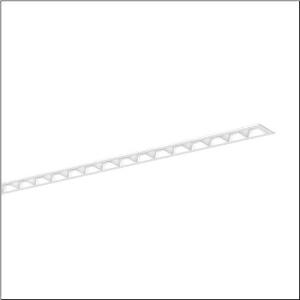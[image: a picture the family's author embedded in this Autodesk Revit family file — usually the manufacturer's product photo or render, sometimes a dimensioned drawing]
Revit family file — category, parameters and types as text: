
# Revit family: silica_r__21_51mx16db45wb_49d2
name_source: partatom
category: Lighting Fixtures
units: mm (PartAtom-declared; Revit-internal decimal feet)

## family parameters
Cut with Voids When Loaded = No
Host = Face
Light Source = No
Part Type = Normal
Room Calculation Point = No
Round Connector Dimension = Use Diameter
Shared = No

## types (1)
- --- (1 x LED, 5400 lm, 29.3 W, 4000K)
    Apparent Load = 29 VA
    CIE Flux Codes = 83 98 100 100 100
    Color Rendering = 80
    Color Temperature = 4000K
    Default Elevation = 1800 mm
    Description = Silica® 21, office luminaire, primary light control with darklight reflector, of PMMA, white, CAT 2 (L<= 3000cd/m²), light emission: direct distribution, primary light characteristic: symmetric, installation type: recessed, LED, rated luminous flux: 5.400lm, luminous efficacy: 184lm/W, light colour: 840, colour temperature: 4000K, with terminal, 3+2-pole, max. 2.5mm², mains connection: 220..240V, AC, 50/60Hz, rated input power: 29.3W, luminaire housing, of aluminium, traffic white (RAL 9016), length: 1.528mm, width: 79mm, height: 53mm, protection rating (complete): IP20, insulation class (complete): insulation class I (protective earthing), certification: CE, permissible operating ambient temperature: 0..+35°C, standard: EN 50419, packaging unit: 1 piece
    Height = 0 mm  [stored 0 ft]
    Lamp = 1 x LED
    Lamp Light Flux = 5400 lm
    Lamp Power = 29.3 W
    Lamp count = 1
    Length = 1527 mm
    Luminous efficacy = 184 lm/W
    Manufacturer = Siteco
    ModVariant = No
    Model = 51MX16DB45WB
    Mounting Place = Ceiling
    Mounting Type = Recessed
    Number of Poles = 1
    OnlyDefault = Yes
    Power Factor = 1
    Product Name = Silica® 21
    Product group = office luminaire | ceiling recessed
    ProductGroupID = 401
    Protection Class = Protection class I
    Protection Degree = IP 20
    RLX_Detail_Level = 1
    RLX_Emergency_Light_Flux = 0 lm
    RLX_Emergency_Type = 0
    RLX_Emergency_Type_DB = No
    RlxData = <blob elided: 39389 chars, md5=4ce8a875>
    Socket = socket
    Standby Power = 0 W
    System Light Flux = 5400 lm
    System Power = 29 W
    Type Comments = factory setting: luminous flux: 100 % | dim-lin: 254 | 336 mA
    Type Image = l_1297786.jpg
    URL = http://relux.com
    VarID = @adj_055157
    Voltage = 0 V
    Weight = 0.00 kg
    Width = 79 mm

note: [stored X ft] marks values corroborated as IEEE doubles in the binary element streams (Revit-internal decimal feet)

## geometry (parser evidence)
native form markers: Blend x4, Sweep x12
no freeform markers — native parametric forms only
